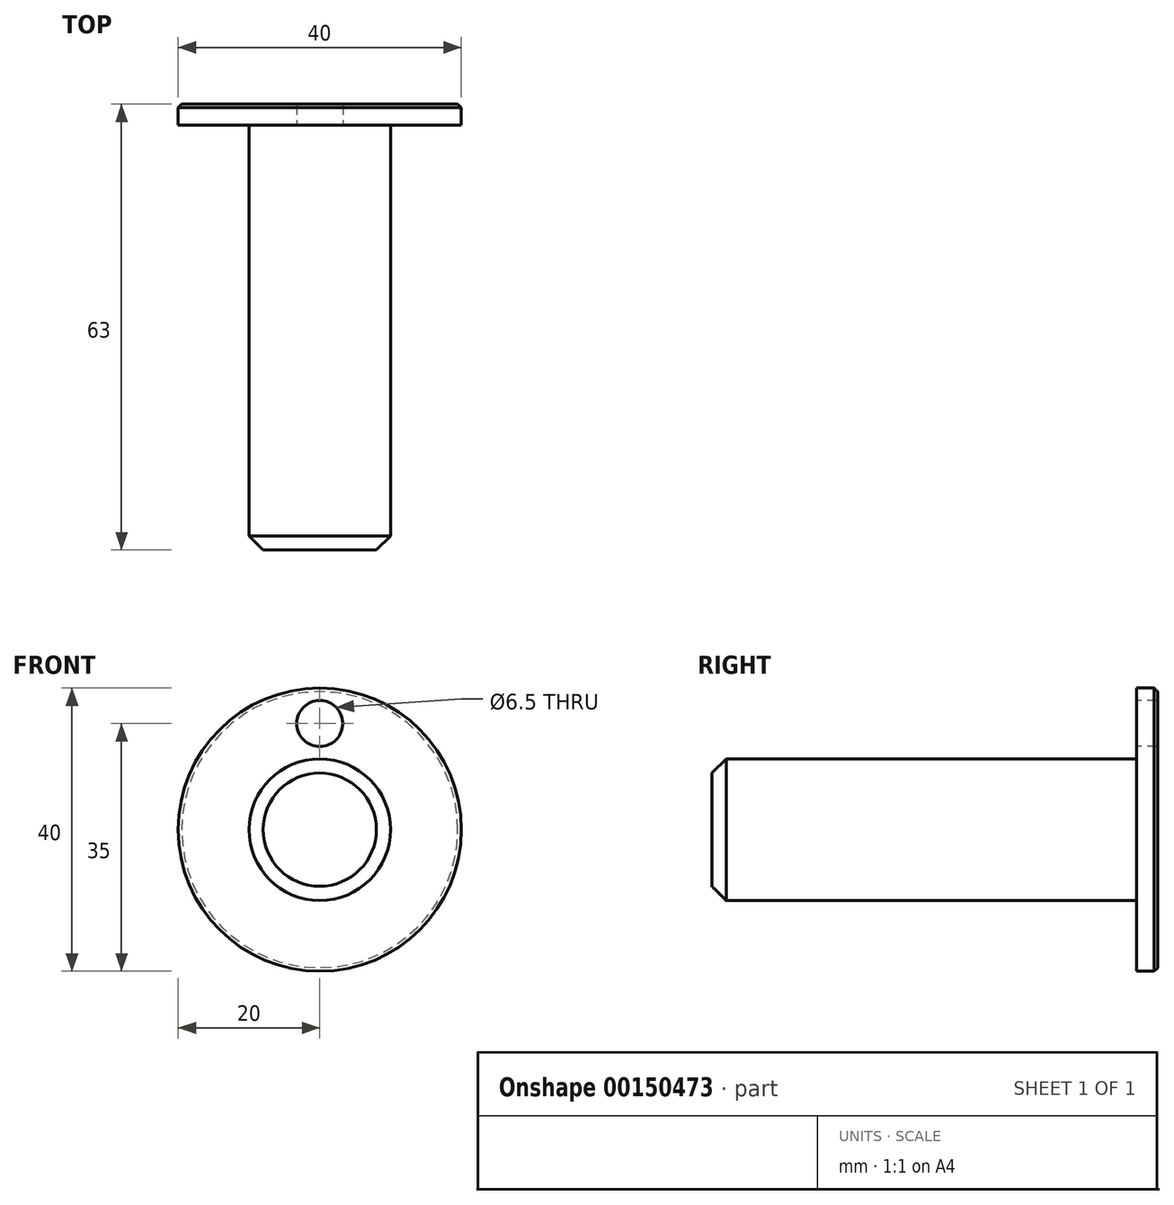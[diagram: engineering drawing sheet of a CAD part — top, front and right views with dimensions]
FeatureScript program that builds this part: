
annotation { "Feature Type Name" : "Feature", "Feature Type Description" : "" }
export const myFeature = defineFeature(function(context is Context, id is Id, definition is map)
    precondition{}
    {
        {
            var Q0;
            Q0=qCreatedBy(makeId("Front.planeOp"),FACE);
            var sketch = newSketch(context, id + "F0", { "sketchPlane" : qUnion([Q0])});
            skCircle(sketch, "E0", {"center": v(0, 0) * mm, "radius": 10 * mm});
            skSolve(sketch);
        }
        {
            var Q0;
            Q0=makeQuery(id+"F0.imprint","IMPRINT",FACE,{"disambiguationData":[TD([[makeQuery(id+"F0.imprint","IMPRINT",EDGE,{"derivedFrom":sQuery(id+"F0.wireOp",EDGE,"E0")}),1.0]])]});
            extrude(context, id + "F1", {"entities" : qUnion([Q0]), "depth" : 60 * mm});
        }
        {
            var Q0;
            Q0=makeQuery(id+"F1.opExtrude","CAP_FACE",FACE,{"disambiguationData":[OSD([sQuery(id+"F0.wireOp",EDGE,"E0")])],"isStart":true});
            var sketch = newSketch(context, id + "F2", { "sketchPlane" : qUnion([Q0])});
            skCircle(sketch, "E1", {"center": v(0, 0) * mm, "radius": 20 * mm});
            skSolve(sketch);
        }
        {
            var Q0;
            Q0=makeQuery(id+"F2.imprint","IMPRINT",FACE,{"disambiguationData":[TD([[makeQuery(id+"F2.imprint","IMPRINT",EDGE,{"derivedFrom":sQuery(id+"F2.wireOp",EDGE,"E1")}),1.0]])]});
            var Q1;
            Q1=makeQuery(id+"F2.imprint","IMPRINT",FACE,{"disambiguationData":[TD([[makeQuery(id+"F2.imprint","IMPRINT",EDGE,{"derivedFrom":makeQuery(id+"F1.opExtrude","CAP_EDGE",EDGE,{"disambiguationData":[OSD([sQuery(id+"F0.wireOp",EDGE,"E0")])],"isStart":true})}),-1.0]])]});
            extrude(context, id + "F3", {"entities" : qUnion([Q0, Q1]), "operationType" : NewBodyOperationType.ADD, "depth" : 3 * mm});
        }
        {
            var Q0;
            Q0=makeQuery(id+"F1.opExtrude","CAP_EDGE",EDGE,{"disambiguationData":[OSD([sQuery(id+"F0.wireOp",EDGE,"E0")])],"isStart":false});
            chamfer(context, id + "F4", {"entities" : qUnion([Q0]), "width" : 2 * mm, "tangentPropagation" : true});
        }
        {
            var Q0;
            Q0=makeQuery(id+"F3.opExtrude","CAP_FACE",FACE,{"disambiguationData":[OSD([sQuery(id+"F2.wireOp",EDGE,"E1")])],"isStart":false});
            var sketch = newSketch(context, id + "F5", { "sketchPlane" : qUnion([Q0])});
            skPoint(sketch, "E2", {"position": v(0, 15) * mm});
            skSolve(sketch);
        }
        {
            var Q0;
            Q0=sQuery(id+"F5.wireOp",VERTEX,"E2");
            var Q1;
            Q1=makeQuery(id+"F1.opExtrude","SWEPT_BODY",BODY,{"disambiguationData":[OSD([sQuery(id+"F0.wireOp",EDGE,"E0")])]});
            hole(context, id + "F6", {"style" : HoleStyle.SIMPLE, "endStyle" : HoleEndStyle.THROUGH, "holeDiameter" : 6.5 * mm, "locations" : qUnion([Q0]), "scope" : qUnion([Q1]), "isTappedThrough" : true, "startStyle" : HoleStartStyle.PART});
        }
        {
            var Q0;
            Q0=makeQuery(id+"F3.opExtrude","CAP_EDGE",EDGE,{"disambiguationData":[OSD([sQuery(id+"F2.wireOp",EDGE,"E1")])],"isStart":false});
            chamfer(context, id + "F7", {"entities" : qUnion([Q0]), "width" : 0.5 * mm, "tangentPropagation" : true});
        }
    });
